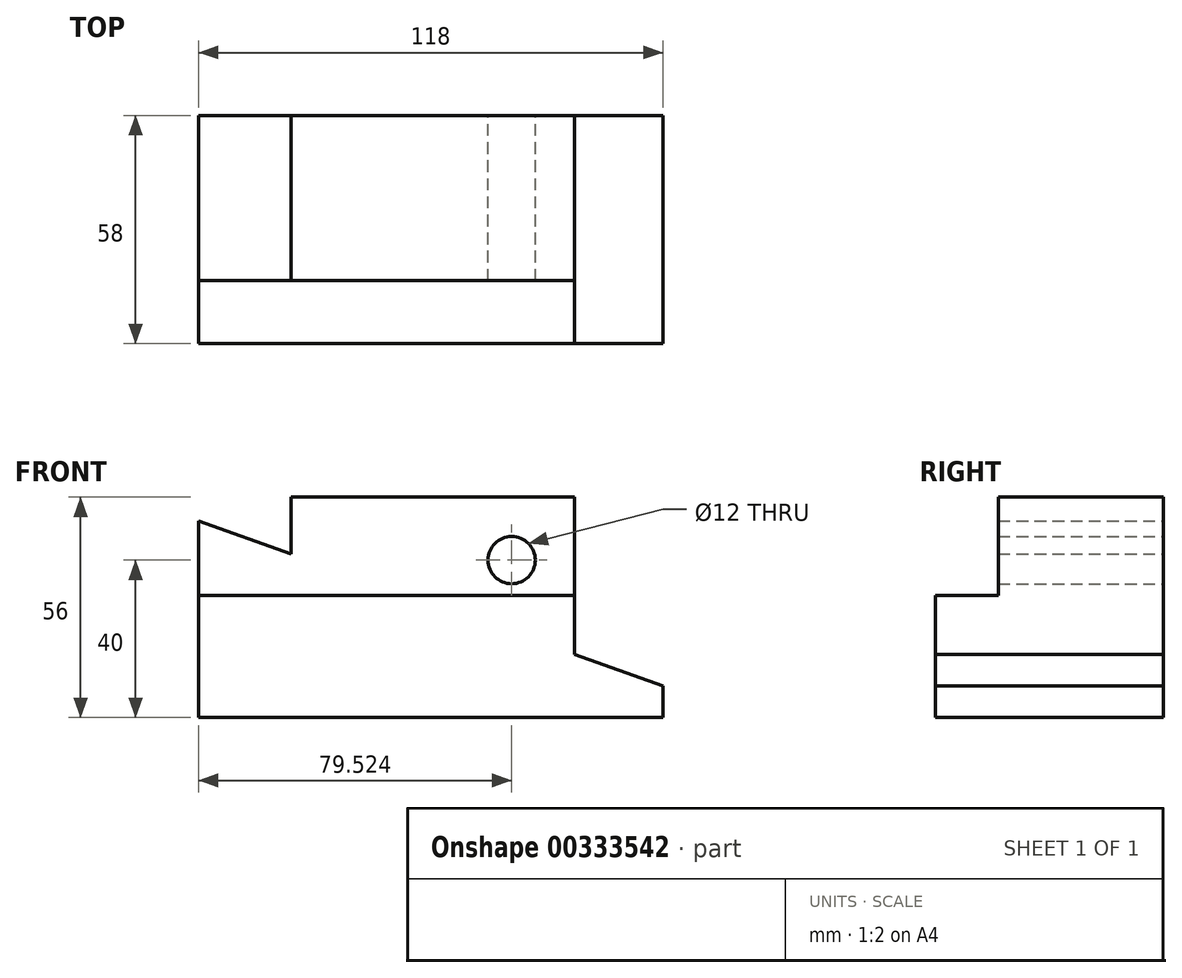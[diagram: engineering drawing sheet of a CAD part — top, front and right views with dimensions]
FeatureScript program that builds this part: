
annotation { "Feature Type Name" : "Feature", "Feature Type Description" : "" }
export const myFeature = defineFeature(function(context is Context, id is Id, definition is map)
    precondition{}
    {
        {
            var Q0;
            Q0=qCreatedBy(makeId("Front.planeOp"),FACE);
            var sketch = newSketch(context, id + "F0", { "sketchPlane" : qUnion([Q0])});
            skLineSegment(sketch, "E0", {"start": v(0, 0) * mm, "end": v(0, 50) * mm});
            skLineSegment(sketch, "E1", {"start": v(0, 50) * mm, "end": v(58, 29.36) * mm});
            skLineSegment(sketch, "E2", {"start": v(58, 29.36) * mm, "end": v(58, 0) * mm});
            skLineSegment(sketch, "E3", {"start": v(58, 0) * mm, "end": v(118, 0) * mm});
            skLineSegment(sketch, "E4", {"start": v(118, 0) * mm, "end": v(118, 8) * mm});
            skLineSegment(sketch, "E5", {"start": v(118, 8) * mm, "end": v(95.52, 16) * mm});
            skLineSegment(sketch, "E6", {"start": v(95.52, 16) * mm, "end": v(95.52, 56) * mm});
            skLineSegment(sketch, "E7", {"start": v(95.52, 56) * mm, "end": v(23.52, 56) * mm});
            skLineSegment(sketch, "E8", {"start": v(23.52, 56) * mm, "end": v(23.52, 41.63) * mm});
            skLineSegment(sketch, "E9", {"start": v(0, 0) * mm, "end": v(58, 0) * mm});
            skCircle(sketch, "E10", {"center": v(79.52, 40) * mm, "radius": 6 * mm});
            skLineSegment(sketch, "E11", {"start": v(58, 29.36) * mm, "end": v(95.52, 16) * mm, "construction": true});
            skSolve(sketch);
        }
        {
            var Q0;
            Q0 = qSketchRegion(id + "F0", true);
            extrude(context, id + "F1", {"entities" : qUnion([Q0]), "depth" : 58 * mm});
        }
        {
            var Q0;
            Q0=makeQuery(id+"F1.opExtrude","SWEPT_FACE",FACE,{"disambiguationData":[OSD([sQuery(id+"F0.wireOp",EDGE,"E7")])]});
            var sketch = newSketch(context, id + "F2", { "sketchPlane" : qUnion([Q0])});
            skLineSegment(sketch, "E12.bottom", {"start": v(0, -42) * mm, "end": v(228.67, -42) * mm});
            skLineSegment(sketch, "E12.top", {"start": v(0, -58) * mm, "end": v(228.67, -58) * mm});
            skLineSegment(sketch, "E12.left", {"start": v(0, -58) * mm, "end": v(0, -42) * mm});
            skLineSegment(sketch, "E12.right", {"start": v(228.67, -58) * mm, "end": v(228.67, -42) * mm});
            skSolve(sketch);
        }
        {
            var Q0;
            Q0 = qSketchRegion(id + "F2", true);
            extrude(context, id + "F3", {"entities" : qUnion([Q0]), "operationType" : NewBodyOperationType.REMOVE, "oppositeDirection" : true, "depth" : 25 * mm});
        }
    });
